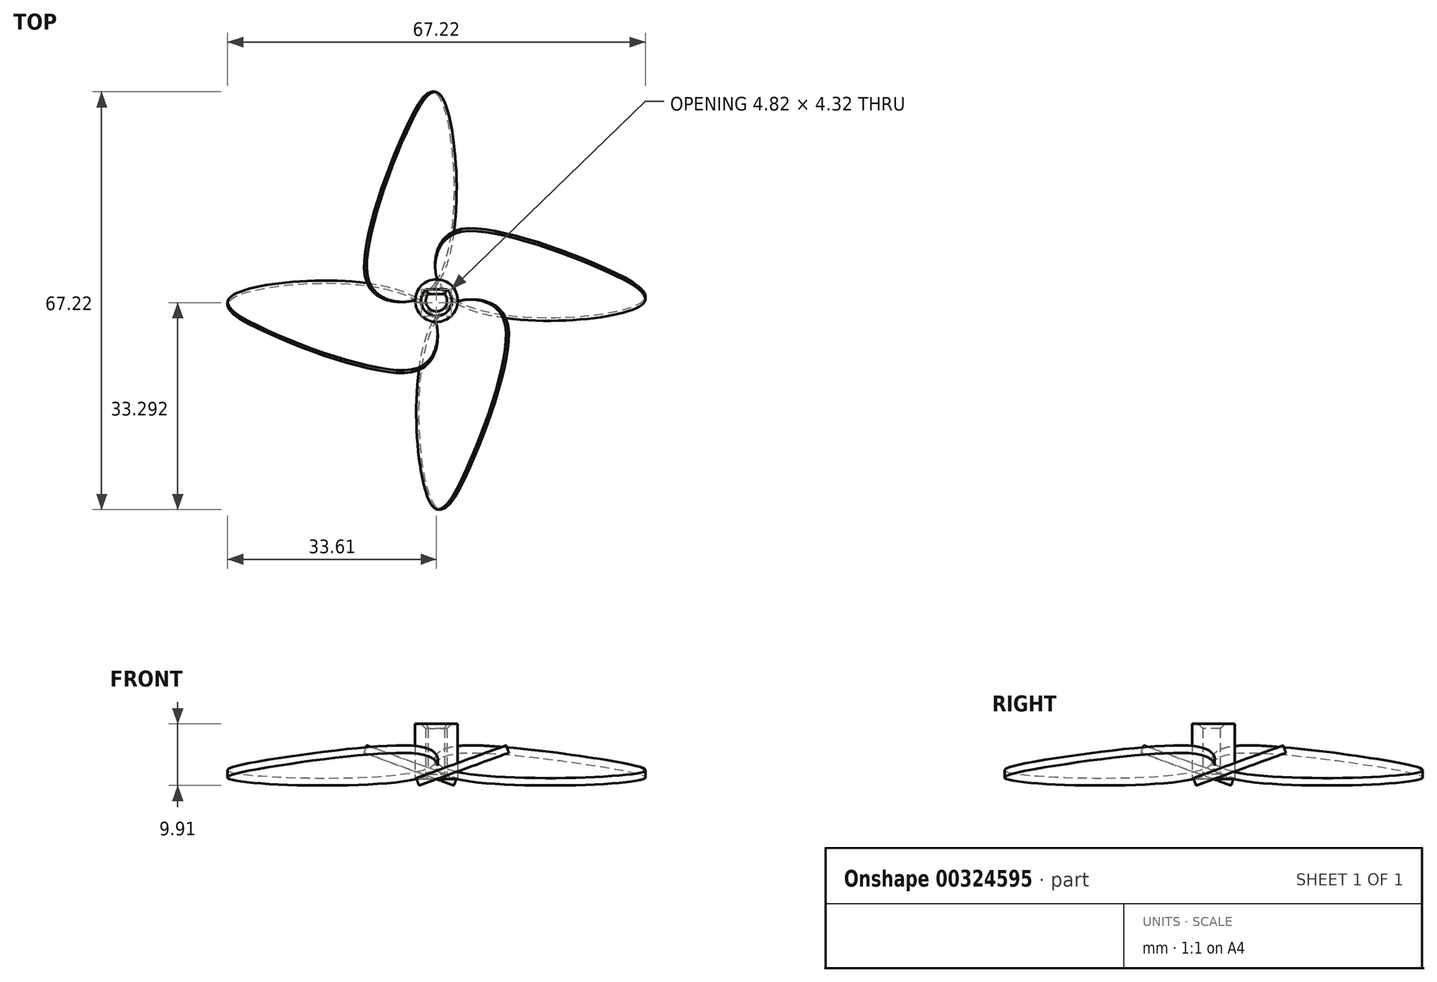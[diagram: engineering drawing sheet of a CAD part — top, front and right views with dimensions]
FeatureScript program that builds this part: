
annotation { "Feature Type Name" : "Feature", "Feature Type Description" : "" }
export const myFeature = defineFeature(function(context is Context, id is Id, definition is map)
    precondition{}
    {
        {
            var Q0;
            Q0=qCreatedBy(makeId("Top.planeOp"),FACE);
            var sketch = newSketch(context, id + "F0", { "sketchPlane" : qUnion([Q0])});
            skCircle(sketch, "E0", {"center": v(0, 0) * mm, "radius": 3.43 * mm});
            skArc(sketch, "E1", {"start": v(-1.33, 1.08) * mm, "mid": v(0, -1.71) * mm, "end": v(1.33, 1.08) * mm});
            skLineSegment(sketch, "E2", {"start": v(-1.33, 1.08) * mm, "end": v(1.33, 1.08) * mm});
            skLineSegment(sketch, "E3", {"start": v(-1.71, 0) * mm, "end": v(0, 0) * mm});
            skLineSegment(sketch, "E4", {"start": v(0, 0) * mm, "end": v(1.71, 0) * mm});
            skLineSegment(sketch, "E5", {"start": v(1.71, 0) * mm, "end": v(2.63, 0) * mm});
            skLineSegment(sketch, "E6", {"start": v(2.63, 0) * mm, "end": v(3.43, 0) * mm});
            skLineSegment(sketch, "E7", {"start": v(-1.71, 0) * mm, "end": v(-3.43, 0) * mm});
            skSolve(sketch);
        }
        {
            var Q0;
            Q0=qSketchRegion(id+"F0",true);
            extrude(context, id + "F1", {"entities" : qUnion([Q0]), "depth" : 8.9 * mm});
        }
        {
            var Q0;
            Q0=qCreatedBy(makeId("Top.planeOp"),FACE);
            var sketch = newSketch(context, id + "F2", { "sketchPlane" : qUnion([Q0])});
            skLineSegment(sketch, "E8", {"start": v(0, 0) * mm, "end": v(44.26, 0) * mm});
            skLineSegment(sketch, "E9", {"start": v(0, 0) * mm, "end": v(0, 37.3) * mm});
            skSolve(sketch);
        }
        {
            var Q0;
            Q0=sQuery(id+"F2.wireOp",EDGE,"E8");
            cPlane(context, id + "F3", {"entities" : qUnion([Q0]), "cplaneType" : CPlaneType.LINE_ANGLE, "offset" : 25.4 * mm, "angle" : 70 * degree, "oppositeDirection" : true, "width" : 152.4 * mm, "height" : 152.4 * mm});
        }
        {
            var Q0;
            Q0=qCreatedBy(id+"F3.planeOp",FACE);
            var sketch = newSketch(context, id + "F4", { "sketchPlane" : qUnion([Q0])});
            skLineSegment(sketch, "E10", {"start": v(3.2, 0) * mm, "end": v(33.3, 0) * mm});
            skLineSegment(sketch, "E11", {"start": v(1.22, -10.66) * mm, "end": v(1.1, -10.51) * mm});
            skPoint(sketch, "E12.2.internal.snap0", {"position": v(2.15, -5.26) * mm});
            skFitSpline(sketch, "E12", {"points": [v(1.1, -10.51) * mm, v(8.74, -12.05) * mm, v(27.8, -5.26) * mm, v(33.3, 0) * mm, v(3.2, 0) * mm, v(1.1, -10.51) * mm]});
            skSolve(sketch);
        }
        {
            var Q0;
            Q0=qSketchRegion(id+"F4",true);
            extrude(context, id + "F5", {"entities" : qUnion([Q0]), "oppositeDirection" : true, "depth" : 1.27 * mm});
        }
        {
            var Q0;
            Q0=makeQuery(id+"F5.opExtrude","SWEPT_BODY",BODY,{"disambiguationData":[OSD([sQuery(id+"F4.wireOp",EDGE,"E10"),sQuery(id+"F4.wireOp",EDGE,"E12")])]});
            var Q1;
            Q1=makeQuery(id+"F1.opExtrude","CAP_EDGE",EDGE,{"disambiguationData":[OSD([sQuery(id+"F0.wireOp",EDGE,"E0")])],"isStart":true});
            circularPattern(context, id + "F6", {"entities" : qUnion([Q0]), "axis" : qUnion([Q1]), "angle" : 360 * degree, "instanceCount" : 4, "equalSpace" : true});
        }
        {
            var Q0;
            Q0=makeQuery(id+"F1.opExtrude","CAP_EDGE",EDGE,{"disambiguationData":[OSD([sQuery(id+"F0.wireOp",EDGE,"E2")])],"isStart":true});
            var Q1;
            Q1=makeQuery(id+"F1.opExtrude","CAP_EDGE",EDGE,{"disambiguationData":[OSD([sQuery(id+"F0.wireOp",EDGE,"E1")])],"isStart":true});
            chamfer(context, id + "F7", {"entities" : qUnion([Q0, Q1]), "width" : 0.76 * mm});
        }
        {
            var Q0;
            Q0=makeQuery(id+"F1.opExtrude","CAP_EDGE",EDGE,{"disambiguationData":[OSD([sQuery(id+"F0.wireOp",EDGE,"E2")])],"isStart":false});
            var Q1;
            Q1=makeQuery(id+"F1.opExtrude","CAP_EDGE",EDGE,{"disambiguationData":[OSD([sQuery(id+"F0.wireOp",EDGE,"E1")])],"isStart":false});
            chamfer(context, id + "F8", {"entities" : qUnion([Q0, Q1]), "width" : 0.76 * mm, "tangentPropagation" : true});
        }
    });
